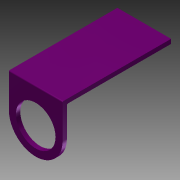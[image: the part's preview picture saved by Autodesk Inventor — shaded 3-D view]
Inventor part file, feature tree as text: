
AUTODESK INVENTOR PART (.ipt)
format: ipt  version: 2015 (Build 190159000, 159)  size: 101,376 bytes
history: native  units: mm
features: sketch x2, extrude x2, fillet x1
ambient origin geometry x8: Origin, YZ Plane, XZ Plane, XY Plane, X Axis, Y Axis, Z Axis, Center Point
bodies: Body1 (feature_tree)
feature tree (5):
  sketch  "Sketch1"  dims[d5=24.75mm d10=50.0mm]
  extrude  "Extrusion4"  Depth=50.0mm
  extrude  "Extrusion5"  Depth=24.75mm
  fillet  "Fillet1"  Radius=24.75mm
  sketch  "Sketch2"  dims[d28=18.25mm d29=24.75mm d30=24.75mm d31=3.45mm d34=2.0mm d35=0.0mm d36=2.0mm d37=0.0mm d53=0.5mm]
